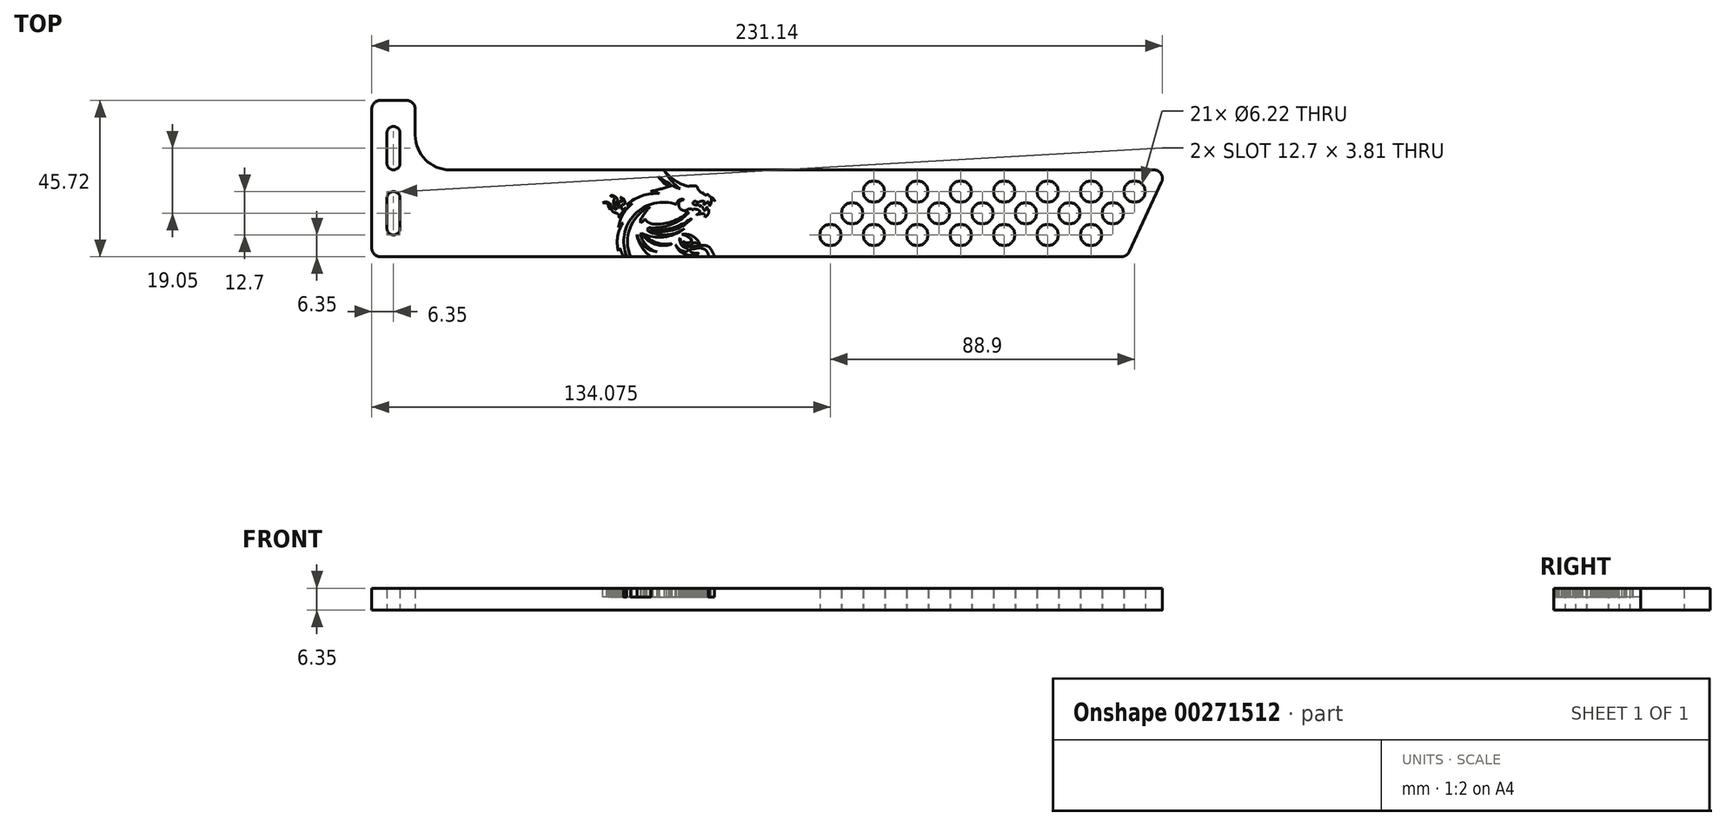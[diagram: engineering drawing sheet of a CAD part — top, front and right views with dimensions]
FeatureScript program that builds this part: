
annotation { "Feature Type Name" : "Feature", "Feature Type Description" : "" }
export const myFeature = defineFeature(function(context is Context, id is Id, definition is map)
    precondition{}
    {
        {
            var Q0;
            Q0=qCreatedBy(makeId("Top.planeOp"),FACE);
            var sketch = newSketch(context, id + "F0", { "sketchPlane" : qUnion([Q0])});
            skLineSegment(sketch, "E0.top", {"start": v(2.54, 45.72) * mm, "end": v(10.16, 45.72) * mm});
            skLineSegment(sketch, "E0.left", {"start": v(0, 2.54) * mm, "end": v(0, 43.18) * mm});
            skLineSegment(sketch, "E0.right", {"start": v(12.7, 35.56) * mm, "end": v(12.7, 43.18) * mm});
            skLineSegment(sketch, "E1.top", {"start": v(22.86, 25.4) * mm, "end": v(228.6, 25.4) * mm});
            skLineSegment(sketch, "E2", {"start": v(2.54, 0) * mm, "end": v(219.12, 0) * mm});
            skArc(sketch, "E3", {"start": v(4.45, 8.25) * mm, "mid": v(6.35, 6.35) * mm, "end": v(8.26, 8.25) * mm});
            skLineSegment(sketch, "E4", {"start": v(4.45, 8.25) * mm, "end": v(4.45, 17.15) * mm});
            skLineSegment(sketch, "E5", {"start": v(8.26, 17.15) * mm, "end": v(8.26, 8.25) * mm});
            skArc(sketch, "E6", {"start": v(8.26, 17.15) * mm, "mid": v(6.35, 19.05) * mm, "end": v(4.45, 17.15) * mm});
            skLineSegment(sketch, "E7.0.1.0", {"start": v(8.26, 36.2) * mm, "end": v(8.26, 27.3) * mm});
            skLineSegment(sketch, "E7.0.1.1", {"start": v(4.45, 27.3) * mm, "end": v(4.45, 36.2) * mm});
            skArc(sketch, "E7.0.1.2", {"start": v(8.26, 36.2) * mm, "mid": v(6.35, 38.1) * mm, "end": v(4.45, 36.2) * mm});
            skArc(sketch, "E7.0.1.3", {"start": v(4.45, 27.3) * mm, "mid": v(6.35, 25.4) * mm, "end": v(8.26, 27.3) * mm});
            skLineSegment(sketch, "E7.direction1", {"start": v(4.45, 8.25) * mm, "end": v(72.67, 8.25) * mm, "construction": true});
            skLineSegment(sketch, "E7.direction2", {"start": v(4.45, 8.25) * mm, "end": v(4.45, 27.3) * mm, "construction": true});
            skPoint(sketch, "E8.visualSharp", {"position": v(0, 45.72) * mm});
            skArc(sketch, "E8.filletArc", {"start": v(2.54, 45.72) * mm, "mid": v(0.74, 44.98) * mm, "end": v(0, 43.18) * mm});
            skPoint(sketch, "E9.visualSharp", {"position": v(12.7, 45.72) * mm});
            skArc(sketch, "E9.filletArc", {"start": v(12.7, 43.18) * mm, "mid": v(11.96, 44.98) * mm, "end": v(10.16, 45.72) * mm});
            skPoint(sketch, "E10.visualSharp", {"position": v(0, 0) * mm});
            skArc(sketch, "E10.filletArc", {"start": v(0, 2.54) * mm, "mid": v(0.74, 0.74) * mm, "end": v(2.54, 0) * mm});
            skPoint(sketch, "E11.visualSharp", {"position": v(12.7, 25.4) * mm});
            skArc(sketch, "E11.filletArc", {"start": v(12.7, 35.56) * mm, "mid": v(15.68, 28.38) * mm, "end": v(22.86, 25.4) * mm});
            skLineSegment(sketch, "E12", {"start": v(221.43, 1.47) * mm, "end": v(230.9, 21.79) * mm});
            skPoint(sketch, "E13.orphan", {"position": v(254, 0) * mm});
            skPoint(sketch, "E14.visualSharp", {"position": v(232.59, 25.4) * mm});
            skArc(sketch, "E14.filletArc", {"start": v(230.9, 21.79) * mm, "mid": v(230.74, 24.22) * mm, "end": v(228.6, 25.4) * mm});
            skPoint(sketch, "E15.visualSharp", {"position": v(220.74, 0) * mm});
            skArc(sketch, "E15.filletArc", {"start": v(219.12, 0) * mm, "mid": v(220.49, 0.4) * mm, "end": v(221.43, 1.47) * mm});
            skCircle(sketch, "E16.1.0.0", {"center": v(210.28, 6.35) * mm, "radius": 3.11 * mm});
            skCircle(sketch, "E16.2.0.0", {"center": v(216.63, 12.7) * mm, "radius": 3.11 * mm});
            skCircle(sketch, "E16.3.0.0", {"center": v(222.98, 19.05) * mm, "radius": 3.11 * mm});
            skLineSegment(sketch, "E17", {"start": v(210.28, 6.35) * mm, "end": v(222.98, 19.05) * mm});
            skCircle(sketch, "E18.1.0.0", {"center": v(203.93, 12.7) * mm, "radius": 3.11 * mm});
            skCircle(sketch, "E18.1.0.1", {"center": v(210.28, 19.05) * mm, "radius": 3.11 * mm});
            skCircle(sketch, "E18.1.0.2", {"center": v(197.58, 6.35) * mm, "radius": 3.11 * mm});
            skCircle(sketch, "E18.2.0.0", {"center": v(191.23, 12.7) * mm, "radius": 3.11 * mm});
            skCircle(sketch, "E18.2.0.1", {"center": v(197.58, 19.05) * mm, "radius": 3.11 * mm});
            skCircle(sketch, "E18.2.0.2", {"center": v(184.88, 6.35) * mm, "radius": 3.11 * mm});
            skLineSegment(sketch, "E18.direction1", {"start": v(216.63, 12.7) * mm, "end": v(203.93, 12.7) * mm, "construction": true});
            skCircle(sketch, "E19.0.3.0", {"center": v(178.53, 12.7) * mm, "radius": 3.11 * mm});
            skCircle(sketch, "E19.2.3.0", {"center": v(184.88, 19.05) * mm, "radius": 3.11 * mm});
            skCircle(sketch, "E19.4.3.0", {"center": v(172.18, 6.35) * mm, "radius": 3.11 * mm});
            skCircle(sketch, "E19.0.4.0", {"center": v(165.83, 12.7) * mm, "radius": 3.11 * mm});
            skCircle(sketch, "E19.2.4.0", {"center": v(172.18, 19.05) * mm, "radius": 3.11 * mm});
            skCircle(sketch, "E19.4.4.0", {"center": v(159.48, 6.35) * mm, "radius": 3.11 * mm});
            skCircle(sketch, "E20.0.5.0", {"center": v(153.13, 12.7) * mm, "radius": 3.11 * mm});
            skCircle(sketch, "E20.2.5.0", {"center": v(159.48, 19.05) * mm, "radius": 3.11 * mm});
            skCircle(sketch, "E20.4.5.0", {"center": v(146.78, 6.35) * mm, "radius": 3.11 * mm});
            skCircle(sketch, "E20.0.6.0", {"center": v(140.43, 12.7) * mm, "radius": 3.11 * mm});
            skCircle(sketch, "E20.2.6.0", {"center": v(146.78, 19.05) * mm, "radius": 3.11 * mm});
            skCircle(sketch, "E20.4.6.0", {"center": v(134.08, 6.35) * mm, "radius": 3.11 * mm});
            skSolve(sketch);
        }
        {
            var Q0;
            Q0=makeQuery(id+"F0.imprint","IMPRINT",FACE,{"disambiguationData":[TD([[makeQuery(id+"F0.imprint","IMPRINT",EDGE,{"derivedFrom":sQuery(id+"F0.wireOp",EDGE,"E0.top")}),-1.0]])]});
            extrude(context, id + "F1", {"entities" : qUnion([Q0]), "depth" : 6.35 * mm});
        }
        {
            var Q0;
            Q0=makeQuery(id+"F1.opExtrude","CAP_FACE",FACE,{"disambiguationData":[OSD([sQuery(id+"F0.wireOp",EDGE,"E0.top"),sQuery(id+"F0.wireOp",EDGE,"E0.left"),sQuery(id+"F0.wireOp",EDGE,"E0.right"),sQuery(id+"F0.wireOp",EDGE,"E1.top"),sQuery(id+"F0.wireOp",EDGE,"E2"),sQuery(id+"F0.wireOp",EDGE,"E3"),sQuery(id+"F0.wireOp",EDGE,"E4"),sQuery(id+"F0.wireOp",EDGE,"E5"),sQuery(id+"F0.wireOp",EDGE,"E6"),sQuery(id+"F0.wireOp",EDGE,"E7.0.1.0"),sQuery(id+"F0.wireOp",EDGE,"E7.0.1.1"),sQuery(id+"F0.wireOp",EDGE,"E7.0.1.2"),sQuery(id+"F0.wireOp",EDGE,"E7.0.1.3"),sQuery(id+"F0.wireOp",EDGE,"E7.0.2.0"),sQuery(id+"F0.wireOp",EDGE,"E7.0.2.1"),sQuery(id+"F0.wireOp",EDGE,"E7.0.2.2"),sQuery(id+"F0.wireOp",EDGE,"E7.0.2.3"),sQuery(id+"F0.wireOp",EDGE,"E8.filletArc"),sQuery(id+"F0.wireOp",EDGE,"E9.filletArc"),sQuery(id+"F0.wireOp",EDGE,"E10.filletArc"),sQuery(id+"F0.wireOp",EDGE,"E11.filletArc"),sQuery(id+"F0.wireOp",EDGE,"XhxQMXou-DX2P-GOic-amz2-HAkX6FaiB0FW"),sQuery(id+"F0.wireOp",EDGE,"E12"),sQuery(id+"F0.wireOp",EDGE,"E14.filletArc"),sQuery(id+"F0.wireOp",EDGE,"E15.filletArc"),sQuery(id+"F0.wireOp",EDGE,"E16.1.0.0"),sQuery(id+"F0.wireOp",EDGE,"E16.2.0.0"),sQuery(id+"F0.wireOp",EDGE,"E16.3.0.0"),sQuery(id+"F0.wireOp",EDGE,"7b475b23-b044-4741-b834-0fa792fca9ea.1.0.0"),sQuery(id+"F0.wireOp",EDGE,"7b475b23-b044-4741-b834-0fa792fca9ea.1.0.1"),sQuery(id+"F0.wireOp",EDGE,"7b475b23-b044-4741-b834-0fa792fca9ea.1.0.2"),sQuery(id+"F0.wireOp",EDGE,"7b475b23-b044-4741-b834-0fa792fca9ea.1.0.3"),sQuery(id+"F0.wireOp",EDGE,"7b475b23-b044-4741-b834-0fa792fca9ea.2.0.0"),sQuery(id+"F0.wireOp",EDGE,"7b475b23-b044-4741-b834-0fa792fca9ea.2.0.1"),sQuery(id+"F0.wireOp",EDGE,"7b475b23-b044-4741-b834-0fa792fca9ea.2.0.2"),sQuery(id+"F0.wireOp",EDGE,"7b475b23-b044-4741-b834-0fa792fca9ea.2.0.3"),sQuery(id+"F0.wireOp",EDGE,"7b475b23-b044-4741-b834-0fa792fca9ea.3.0.0"),sQuery(id+"F0.wireOp",EDGE,"7b475b23-b044-4741-b834-0fa792fca9ea.3.0.1"),sQuery(id+"F0.wireOp",EDGE,"7b475b23-b044-4741-b834-0fa792fca9ea.3.0.2"),sQuery(id+"F0.wireOp",EDGE,"7b475b23-b044-4741-b834-0fa792fca9ea.3.0.3"),sQuery(id+"F0.wireOp",EDGE,"7b475b23-b044-4741-b834-0fa792fca9ea.4.0.0"),sQuery(id+"F0.wireOp",EDGE,"7b475b23-b044-4741-b834-0fa792fca9ea.4.0.1"),sQuery(id+"F0.wireOp",EDGE,"7b475b23-b044-4741-b834-0fa792fca9ea.4.0.2"),sQuery(id+"F0.wireOp",EDGE,"7b475b23-b044-4741-b834-0fa792fca9ea.4.0.3"),sQuery(id+"F0.wireOp",EDGE,"7b475b23-b044-4741-b834-0fa792fca9ea.5.0.0"),sQuery(id+"F0.wireOp",EDGE,"7b475b23-b044-4741-b834-0fa792fca9ea.5.0.1"),sQuery(id+"F0.wireOp",EDGE,"7b475b23-b044-4741-b834-0fa792fca9ea.5.0.2"),sQuery(id+"F0.wireOp",EDGE,"7b475b23-b044-4741-b834-0fa792fca9ea.5.0.3"),sQuery(id+"F0.wireOp",EDGE,"7b475b23-b044-4741-b834-0fa792fca9ea.6.0.0"),sQuery(id+"F0.wireOp",EDGE,"7b475b23-b044-4741-b834-0fa792fca9ea.6.0.1"),sQuery(id+"F0.wireOp",EDGE,"7b475b23-b044-4741-b834-0fa792fca9ea.6.0.2"),sQuery(id+"F0.wireOp",EDGE,"7b475b23-b044-4741-b834-0fa792fca9ea.6.0.3"),sQuery(id+"F0.wireOp",EDGE,"7b475b23-b044-4741-b834-0fa792fca9ea.7.0.0"),sQuery(id+"F0.wireOp",EDGE,"7b475b23-b044-4741-b834-0fa792fca9ea.7.0.1"),sQuery(id+"F0.wireOp",EDGE,"7b475b23-b044-4741-b834-0fa792fca9ea.7.0.2"),sQuery(id+"F0.wireOp",EDGE,"7b475b23-b044-4741-b834-0fa792fca9ea.7.0.3")])],"isStart":false});
            var sketch = newSketch(context, id + "F2", { "sketchPlane" : qUnion([Q0])});
            skLineSegment(sketch, "E21", {"start": v(111.91, 22.02) * mm, "end": v(124.7, 22.02) * mm, "construction": true});
            skLineSegment(sketch, "E22", {"start": v(93.12, 22.02) * mm, "end": v(93.12, 3.84) * mm, "construction": true});
            skEllipticalArc(sketch, "E23", {});
            skEllipticalArc(sketch, "E24", {});
            skEllipticalArc(sketch, "E25", {});
            skEllipticalArc(sketch, "E26", {});
            skEllipticalArc(sketch, "E27", {});
            skLineSegment(sketch, "E28", {"start": v(118.27, 15.08) * mm, "end": v(118.27, 1.13) * mm, "construction": true});
            skLineSegment(sketch, "E29", {"start": v(118.1, 18.88) * mm, "end": v(119.03, 21.76) * mm});
            skLineSegment(sketch, "E30", {"start": v(119.18, 21.85) * mm, "end": v(121.5, 21.29) * mm});
            skLineSegment(sketch, "E31", {"start": v(118.65, 18.87) * mm, "end": v(119.4, 21.28) * mm});
            skLineSegment(sketch, "E32", {"start": v(119.4, 21.28) * mm, "end": v(121.42, 20.8) * mm});
            skArc(sketch, "E33", {"start": v(121.42, 20.8) * mm, "mid": v(123.83, 20.65) * mm, "end": v(121.5, 21.29) * mm});
            skPoint(sketch, "E34.visualSharp", {"position": v(119.07, 21.88) * mm});
            skArc(sketch, "E34.filletArc", {"start": v(119.18, 21.85) * mm, "mid": v(119.1, 21.84) * mm, "end": v(119.03, 21.76) * mm});
            skEllipticalArc(sketch, "E35.MirrorC", {});
            skEllipticalArc(sketch, "E36.MirrorC", {});
            skEllipticalArc(sketch, "E37.MirrorC", {});
            skEllipticalArc(sketch, "E38.trimOffspring", {});
            skEllipticalArc(sketch, "E39.trimOffspring", {});
            skEllipticalArc(sketch, "E40.trimOffspring", {});
            skEllipticalArc(sketch, "E41.trimOffspring", {});
            skLineSegment(sketch, "E42", {"start": v(114.26, 4.24) * mm, "end": v(122.28, 4.24) * mm});
            skEllipticalArc(sketch, "E43.trimOffspring", {});
            skEllipticalArc(sketch, "E44.trimOffspring", {});
            const initialGuessF2  = {"E23": [0.11826750014340877, 0.015082236187587153, 1, 0, 0.005703495972769829, 0.0037955942462822865, 0.8087704461165538, 1.5034823753486115], "E24": [0.11324217923710486, 0.016877323040055132, 0.6434269031423131, 0.7655075573191243, 0.0014490525433377987, 0.001291077385108787, 6.111264569809005, 3.417254100186137], "E25": [0.11827889440944792, 0.009972261073122948, 0, -1, 0.005924312397835806, 0.003007138479654591, 4.399738749622363, 4.432740366885451], "E26": [0.11598712096354366, 0.008977077922474014, -0.9787598014009283, -0.20501036842466144, 0.0019139277871180575, 0.002698036256528401, 4.736724992915178, 1.238121732901221], "E27": [0.11594034994384646, 0.004500067601035371, 0, 1, 0.001621391624212265, 0.0017068755273229488, 6.251739863279235, 1.7313232782154366], "E35.MirrorC": [0.12054787932327389, 0.008977077922474014, 0.9787598014009283, -0.20501036842466142, 0.0019139277871180575, 0.002698036256528401, 5.058073293251867, 1.5337046518671746], "E36.MirrorC": [0.1205946503429711, 0.004500067601035371, 0, 1, 0.001621391624212265, 0.0017068755273229488, 4.551862028964148, 0.017952745052430608], "E37.MirrorC": [0.12329282104971269, 0.016877323040055126, -0.6434269031423131, 0.7655075573191243, 0.0014490525433377987, 0.001291077385108787, 2.865931206993587, 0.1719207373705861], "E38.trimOffspring": [0.11826750014340877, 0.015082236187587153, 1, 0, 0.005703495972769829, 0.0037955942462822865, 3.009051899793022, 4.189151464437954], "E39.trimOffspring": [0.11826750014340878, 0.015082236187587153, 1, 0, 0.005703495972769829, 0.0037955942462822865, 5.239969362590084, 0.13254075379676966], "E40.trimOffspring": [0.11827889440944792, 0.009972261073122948, 0, -1, 0.005924312397835806, 0.003007138479654591, 1.849384891635883, 1.8849135611477357], "E41.trimOffspring": [0.11827889440944792, 0.009972261073122948, 0, -1, 0.005924312397835806, 0.003007138479654591, 5.36960796932527, 5.420151204194051], "E43.trimOffspring": [0.11827889440944721, 0.009972261073122518, 0, -1, 0.005924312397837639, 0.003007138479654591, 0.8631541220241196, 0.9149872669766339], "E44.trimOffspring": [0.11826750014340877, 0.015082236187587153, 1, 0, 0.005703495972769829, 0.0037955942462822865, 1.6014334170188662, 2.332822207473239]};
            skSetInitialGuess(sketch, initialGuessF2);
            skSolve(sketch);
        }
        {
            var Q0;
            Q0=makeQuery(id+"F2.imprint","IMPRINT",FACE,{"disambiguationData":[TD([[makeQuery(id+"F2.imprint","IMPRINT",EDGE,{"derivedFrom":makeQuery(id+"F1.opExtrude","CAP_EDGE",EDGE,{"disambiguationData":[OSD([sQuery(id+"F0.wireOp",EDGE,"E0.top")])],"isStart":false})}),-1.0]])]});
            var sketch = newSketch(context, id + "F3", { "sketchPlane" : qUnion([Q0])});
            skArc(sketch, "E45", {"start": v(72.48, 2.55) * mm, "mid": v(73.02, 1.27) * mm, "end": v(73.6, 0) * mm});
            skArc(sketch, "E46", {"start": v(72.48, 2.55) * mm, "mid": v(72.2, 2.15) * mm, "end": v(72.13, 1.67) * mm});
            skArc(sketch, "E47", {"start": v(73.48, 9.82) * mm, "mid": v(71.88, 5.9) * mm, "end": v(72.13, 1.67) * mm});
            skArc(sketch, "E48", {"start": v(73.48, 9.82) * mm, "mid": v(72.63, 9.33) * mm, "end": v(72.13, 8.48) * mm});
            skArc(sketch, "E49", {"start": v(76.2, 15.57) * mm, "mid": v(73.43, 12.44) * mm, "end": v(72.13, 8.48) * mm});
            skArc(sketch, "E50", {"start": v(74.57, 15.13) * mm, "mid": v(75.39, 15.33) * mm, "end": v(76.2, 15.57) * mm});
            skArc(sketch, "E51", {"start": v(84.06, 18.47) * mm, "mid": v(78.96, 17.82) * mm, "end": v(74.57, 15.13) * mm});
            skArc(sketch, "E52", {"start": v(84.06, 18.47) * mm, "mid": v(82.8, 18.96) * mm, "end": v(81.44, 19.07) * mm});
            skArc(sketch, "E53", {"start": v(81.44, 19.07) * mm, "mid": v(84.66, 19.87) * mm, "end": v(87.8, 20.9) * mm});
            skArc(sketch, "E54", {"start": v(87.8, 20.9) * mm, "mid": v(88.9, 20.26) * mm, "end": v(90.15, 19.94) * mm});
            skArc(sketch, "E55", {"start": v(95.08, 20.56) * mm, "mid": v(93.83, 20.76) * mm, "end": v(92.58, 20.56) * mm});
            skArc(sketch, "E56", {"start": v(95.08, 20.56) * mm, "mid": v(95.57, 19.48) * mm, "end": v(96.43, 18.66) * mm});
            skArc(sketch, "E57", {"start": v(96.43, 18.66) * mm, "mid": v(96.74, 18.59) * mm, "end": v(97.05, 18.66) * mm});
            skArc(sketch, "E58", {"start": v(97.05, 18.66) * mm, "mid": v(97.3, 18.12) * mm, "end": v(97.9, 18.09) * mm});
            skArc(sketch, "E59", {"start": v(98.6, 17.93) * mm, "mid": v(98.29, 18.15) * mm, "end": v(97.9, 18.09) * mm});
            skArc(sketch, "E60", {"start": v(98.6, 17.93) * mm, "mid": v(98.87, 17.55) * mm, "end": v(99.31, 17.38) * mm});
            skArc(sketch, "E61", {"start": v(100.3, 16.31) * mm, "mid": v(99.87, 16.9) * mm, "end": v(99.31, 17.38) * mm});
            skArc(sketch, "E62", {"start": v(100.3, 16.31) * mm, "mid": v(99.8, 16.7) * mm, "end": v(99.25, 17.03) * mm});
            skArc(sketch, "E63", {"start": v(98.72, 14.77) * mm, "mid": v(99.23, 15.84) * mm, "end": v(99.25, 17.03) * mm});
            skArc(sketch, "E64", {"start": v(98.72, 14.77) * mm, "mid": v(98.63, 15.5) * mm, "end": v(98.33, 16.16) * mm});
            skArc(sketch, "E65", {"start": v(96.94, 15.24) * mm, "mid": v(97.72, 15.58) * mm, "end": v(98.33, 16.16) * mm});
            skArc(sketch, "E66", {"start": v(96.94, 15.24) * mm, "mid": v(97.2, 15.67) * mm, "end": v(97.25, 16.16) * mm});
            skArc(sketch, "E67", {"start": v(97.25, 16.16) * mm, "mid": v(96.15, 16.17) * mm, "end": v(95.2, 15.6) * mm});
            skArc(sketch, "E68", {"start": v(94.86, 16.31) * mm, "mid": v(95, 15.94) * mm, "end": v(95.2, 15.6) * mm});
            skArc(sketch, "E69", {"start": v(94.86, 16.31) * mm, "mid": v(94.21, 16.16) * mm, "end": v(93.85, 15.6) * mm});
            skArc(sketch, "E70", {"start": v(93.85, 15.6) * mm, "mid": v(94.6, 15.13) * mm, "end": v(95.47, 15.24) * mm});
            skArc(sketch, "E71", {"start": v(95.47, 15.24) * mm, "mid": v(95.71, 14.96) * mm, "end": v(95.96, 14.69) * mm});
            skArc(sketch, "E72", {"start": v(95.96, 14.69) * mm, "mid": v(96.01, 14.89) * mm, "end": v(96.06, 15.1) * mm});
            skArc(sketch, "E73", {"start": v(97.2, 13.47) * mm, "mid": v(96.74, 14.35) * mm, "end": v(96.06, 15.1) * mm});
            skArc(sketch, "E74", {"start": v(97.2, 13.47) * mm, "mid": v(97.76, 13.88) * mm, "end": v(97.86, 14.56) * mm});
            skArc(sketch, "E75", {"start": v(98.12, 13.58) * mm, "mid": v(98.12, 14.1) * mm, "end": v(97.86, 14.56) * mm});
            skArc(sketch, "E76", {"start": v(98.5, 13.9) * mm, "mid": v(98.3, 13.75) * mm, "end": v(98.12, 13.58) * mm});
            skArc(sketch, "E77", {"start": v(97.3, 11.58) * mm, "mid": v(98.36, 12.5) * mm, "end": v(98.5, 13.9) * mm});
            skArc(sketch, "E78", {"start": v(97.3, 11.58) * mm, "mid": v(97.44, 12.14) * mm, "end": v(97.05, 12.55) * mm});
            skArc(sketch, "E79", {"start": v(97.05, 12.55) * mm, "mid": v(95.97, 12.5) * mm, "end": v(94.93, 12.24) * mm});
            skArc(sketch, "E80", {"start": v(94.93, 12.24) * mm, "mid": v(95.54, 12.7) * mm, "end": v(95.96, 13.33) * mm});
            skArc(sketch, "E81", {"start": v(95.96, 13.33) * mm, "mid": v(95.11, 13.82) * mm, "end": v(94.13, 13.9) * mm});
            skArc(sketch, "E82", {"start": v(93.51, 13.9) * mm, "mid": v(93.82, 13.75) * mm, "end": v(94.13, 13.9) * mm});
            skArc(sketch, "E83", {"start": v(93.51, 13.9) * mm, "mid": v(92.78, 13.98) * mm, "end": v(92.12, 13.66) * mm});
            skArc(sketch, "E84", {"start": v(89.89, 15.95) * mm, "mid": v(90.18, 14) * mm, "end": v(92.12, 13.66) * mm});
            skArc(sketch, "E85", {"start": v(91.29, 16.73) * mm, "mid": v(90.53, 16.45) * mm, "end": v(89.89, 15.95) * mm});
            skArc(sketch, "E86", {"start": v(91.29, 16.73) * mm, "mid": v(89.81, 16.56) * mm, "end": v(89.12, 15.24) * mm});
            skArc(sketch, "E87", {"start": v(89.12, 15.24) * mm, "mid": v(76.85, 12.38) * mm, "end": v(74.54, 0) * mm});
            skArc(sketch, "E88", {"start": v(81.27, 14.56) * mm, "mid": v(75.52, 8.41) * mm, "end": v(75.62, 0) * mm});
            skArc(sketch, "E89", {"start": v(81.27, 14.56) * mm, "mid": v(79.82, 12.75) * mm, "end": v(78.6, 10.79) * mm});
            skArc(sketch, "E90", {"start": v(78.6, 10.79) * mm, "mid": v(78.6, 10.37) * mm, "end": v(78.6, 9.95) * mm});
            skArc(sketch, "E91", {"start": v(78.6, 9.95) * mm, "mid": v(79.36, 10.39) * mm, "end": v(79.86, 11.1) * mm});
            skArc(sketch, "E92", {"start": v(79.83, 11.04) * mm, "mid": v(80.95, 9.98) * mm, "end": v(82.43, 9.53) * mm});
            skArc(sketch, "E93", {"start": v(82.43, 9.53) * mm, "mid": v(87.75, 10.23) * mm, "end": v(92.36, 13) * mm});
            skArc(sketch, "E94", {"start": v(92.5, 12.72) * mm, "mid": v(92.58, 12.93) * mm, "end": v(92.36, 13) * mm});
            skArc(sketch, "E95", {"start": v(81.5, 8.47) * mm, "mid": v(87.47, 9.38) * mm, "end": v(92.5, 12.72) * mm});
            skArc(sketch, "E96", {"start": v(81.5, 8.47) * mm, "mid": v(80.92, 8.38) * mm, "end": v(80.48, 8) * mm});
            skArc(sketch, "E97", {"start": v(80.48, 8) * mm, "mid": v(81.22, 7.23) * mm, "end": v(82.22, 6.86) * mm});
            skArc(sketch, "E98", {"start": v(82.22, 6.86) * mm, "mid": v(86.99, 6.5) * mm, "end": v(91.44, 8.24) * mm});
            skArc(sketch, "E99", {"start": v(78.89, 6.86) * mm, "mid": v(85.36, 5.76) * mm, "end": v(91.44, 8.24) * mm});
            skArc(sketch, "E100", {"start": v(81.76, 8) * mm, "mid": v(87.85, 8.39) * mm, "end": v(93.3, 11.12) * mm});
            skArc(sketch, "E101", {"start": v(93.41, 10.93) * mm, "mid": v(93.38, 11.04) * mm, "end": v(93.3, 11.12) * mm});
            skArc(sketch, "E102", {"start": v(81.76, 7.58) * mm, "mid": v(88, 7.78) * mm, "end": v(93.41, 10.93) * mm});
            skArc(sketch, "E103", {"start": v(81.76, 8) * mm, "mid": v(81.68, 7.79) * mm, "end": v(81.76, 7.58) * mm});
            skArc(sketch, "E104", {"start": v(79.94, 6.17) * mm, "mid": v(79.57, 6.23) * mm, "end": v(79.57, 5.86) * mm});
            skArc(sketch, "E105", {"start": v(79.94, 6.17) * mm, "mid": v(83.37, 4.05) * mm, "end": v(87.4, 3.77) * mm});
            skArc(sketch, "E106", {"start": v(87.4, 3.59) * mm, "mid": v(87.56, 3.68) * mm, "end": v(87.4, 3.77) * mm});
            skArc(sketch, "E107", {"start": v(79.57, 5.86) * mm, "mid": v(83.15, 3.57) * mm, "end": v(87.4, 3.59) * mm});
            skArc(sketch, "E108", {"start": v(78.89, 6.86) * mm, "mid": v(78.6, 6.58) * mm, "end": v(78.62, 6.17) * mm});
            skArc(sketch, "E109", {"start": v(78.62, 6.17) * mm, "mid": v(80.41, 3.18) * mm, "end": v(83.4, 1.4) * mm});
            skArc(sketch, "E110", {"start": v(77.5, 6.46) * mm, "mid": v(79.67, 3.01) * mm, "end": v(83.4, 1.4) * mm});
            skArc(sketch, "E111", {"start": v(77.5, 6.46) * mm, "mid": v(78.93, 2.81) * mm, "end": v(81.64, 0) * mm});
            skArc(sketch, "E112", {"start": v(88.76, 3.62) * mm, "mid": v(89.86, 2.2) * mm, "end": v(91.52, 1.5) * mm});
            skArc(sketch, "E113", {"start": v(91.52, 1.5) * mm, "mid": v(92.3, 1.69) * mm, "end": v(92.08, 2.46) * mm});
            skArc(sketch, "E114", {"start": v(90.1, 5.53) * mm, "mid": v(90.44, 3.57) * mm, "end": v(92.08, 2.46) * mm});
            skArc(sketch, "E115", {"start": v(90.1, 5.53) * mm, "mid": v(91.4, 3.4) * mm, "end": v(93.86, 2.93) * mm});
            skArc(sketch, "E116", {"start": v(96.06, 3.2) * mm, "mid": v(94.95, 3.1) * mm, "end": v(93.86, 2.93) * mm});
            skArc(sketch, "E117", {"start": v(98.65, 2.8) * mm, "mid": v(97.4, 3.3) * mm, "end": v(96.06, 3.2) * mm});
            skArc(sketch, "E118", {"start": v(100.16, 0) * mm, "mid": v(99.57, 1.5) * mm, "end": v(98.65, 2.8) * mm});
            skArc(sketch, "E119", {"start": v(98.4, 0) * mm, "mid": v(97.73, 1.81) * mm, "end": v(95.92, 2.47) * mm});
            skArc(sketch, "E120", {"start": v(95.92, 2.47) * mm, "mid": v(95.1, 2.48) * mm, "end": v(94.3, 2.3) * mm});
            skArc(sketch, "E121", {"start": v(93.11, 2.3) * mm, "mid": v(93.7, 2.28) * mm, "end": v(94.3, 2.3) * mm});
            skArc(sketch, "E122", {"start": v(93.11, 2.3) * mm, "mid": v(93.08, 1.88) * mm, "end": v(93.2, 1.46) * mm});
            skArc(sketch, "E123", {"start": v(93.2, 1.46) * mm, "mid": v(94.28, 1.05) * mm, "end": v(95.45, 1.07) * mm});
            skArc(sketch, "E124", {"start": v(95.45, 0.88) * mm, "mid": v(95.5, 0.98) * mm, "end": v(95.45, 1.07) * mm});
            skArc(sketch, "E125", {"start": v(88.76, 3.62) * mm, "mid": v(91.49, 0.73) * mm, "end": v(95.45, 0.88) * mm});
            skArc(sketch, "E126", {"start": v(95.92, 3.62) * mm, "mid": v(93.77, 6) * mm, "end": v(90.6, 6.54) * mm});
            skArc(sketch, "E127", {"start": v(93.57, 4.95) * mm, "mid": v(92.22, 5.98) * mm, "end": v(90.6, 6.54) * mm});
            skArc(sketch, "E128", {"start": v(91.26, 4.41) * mm, "mid": v(92.56, 4.05) * mm, "end": v(93.57, 4.95) * mm});
            skArc(sketch, "E129", {"start": v(91.26, 4.41) * mm, "mid": v(91.11, 4.41) * mm, "end": v(91.12, 4.27) * mm});
            skArc(sketch, "E130", {"start": v(91.12, 4.27) * mm, "mid": v(92.32, 3.44) * mm, "end": v(93.78, 3.34) * mm});
            skArc(sketch, "E131", {"start": v(93.78, 4.06) * mm, "mid": v(93.56, 3.7) * mm, "end": v(93.78, 3.34) * mm});
            skArc(sketch, "E132", {"start": v(95.92, 3.62) * mm, "mid": v(94.88, 4) * mm, "end": v(93.78, 4.06) * mm});
            skArc(sketch, "E133", {"start": v(84.21, 23.14) * mm, "mid": v(83.97, 23.23) * mm, "end": v(84.05, 22.99) * mm});
            skArc(sketch, "E134", {"start": v(84.21, 23.14) * mm, "mid": v(85.74, 22.13) * mm, "end": v(87.38, 21.29) * mm});
            skArc(sketch, "E135", {"start": v(86.8, 20.74) * mm, "mid": v(87.15, 20.95) * mm, "end": v(87.38, 21.29) * mm});
            skArc(sketch, "E136", {"start": v(86.16, 20.9) * mm, "mid": v(86.46, 20.76) * mm, "end": v(86.8, 20.74) * mm});
            skArc(sketch, "E137", {"start": v(84.05, 22.99) * mm, "mid": v(85.07, 21.9) * mm, "end": v(86.16, 20.9) * mm});
            skLineSegment(sketch, "E138", {"start": v(98.4, 0) * mm, "end": v(100.16, 0) * mm});
            skArc(sketch, "E139", {"start": v(69.99, 17.9) * mm, "mid": v(69.85, 17.8) * mm, "end": v(69.97, 17.67) * mm});
            skArc(sketch, "E140", {"start": v(71.91, 16.42) * mm, "mid": v(71.24, 17.54) * mm, "end": v(69.99, 17.9) * mm});
            skArc(sketch, "E141", {"start": v(71.91, 16.42) * mm, "mid": v(71.73, 16.38) * mm, "end": v(71.62, 16.24) * mm});
            skArc(sketch, "E142", {"start": v(71.62, 16.24) * mm, "mid": v(71.71, 15.22) * mm, "end": v(72.16, 14.3) * mm});
            skArc(sketch, "E143", {"start": v(72.16, 14.3) * mm, "mid": v(72.31, 14.33) * mm, "end": v(72.34, 14.48) * mm});
            skArc(sketch, "E144", {"start": v(72.34, 15.91) * mm, "mid": v(72.26, 15.2) * mm, "end": v(72.34, 14.48) * mm});
            skArc(sketch, "E145", {"start": v(72.54, 16.28) * mm, "mid": v(72.42, 16.1) * mm, "end": v(72.34, 15.91) * mm});
            skArc(sketch, "E146", {"start": v(73.2, 16.04) * mm, "mid": v(72.9, 16.23) * mm, "end": v(72.54, 16.28) * mm});
            skArc(sketch, "E147", {"start": v(73.2, 16.04) * mm, "mid": v(73.32, 16.3) * mm, "end": v(73.28, 16.58) * mm});
            skArc(sketch, "E148", {"start": v(73.28, 16.58) * mm, "mid": v(72.99, 17.02) * mm, "end": v(72.6, 17.38) * mm});
            skArc(sketch, "E149", {"start": v(74.03, 15.76) * mm, "mid": v(73.63, 16.85) * mm, "end": v(72.6, 17.38) * mm});
            skArc(sketch, "E150", {"start": v(73.4, 15.24) * mm, "mid": v(73.83, 15.36) * mm, "end": v(74.03, 15.76) * mm});
            skArc(sketch, "E151", {"start": v(73.4, 15.24) * mm, "mid": v(73.16, 15.18) * mm, "end": v(73.1, 14.94) * mm});
            skArc(sketch, "E152", {"start": v(73.1, 14.94) * mm, "mid": v(72.96, 14.3) * mm, "end": v(73.28, 13.72) * mm});
            skArc(sketch, "E153", {"start": v(73.28, 13.72) * mm, "mid": v(73.64, 13.85) * mm, "end": v(73.92, 14.11) * mm});
            skArc(sketch, "E154", {"start": v(74.2, 14.18) * mm, "mid": v(74.05, 14.18) * mm, "end": v(73.92, 14.11) * mm});
            skArc(sketch, "E155", {"start": v(74.2, 14.01) * mm, "mid": v(74.24, 14.1) * mm, "end": v(74.2, 14.18) * mm});
            skArc(sketch, "E156", {"start": v(74.2, 14.01) * mm, "mid": v(73.12, 12.88) * mm, "end": v(72.39, 11.5) * mm});
            skArc(sketch, "E157", {"start": v(72.22, 11.66) * mm, "mid": v(72.27, 11.55) * mm, "end": v(72.39, 11.5) * mm});
            skArc(sketch, "E158", {"start": v(72.22, 11.66) * mm, "mid": v(72.3, 12.08) * mm, "end": v(72.1, 12.45) * mm});
            skArc(sketch, "E159", {"start": v(72.1, 12.45) * mm, "mid": v(71.4, 12.78) * mm, "end": v(70.67, 13) * mm});
            skArc(sketch, "E160", {"start": v(70.01, 13.82) * mm, "mid": v(70.3, 13.38) * mm, "end": v(70.67, 13) * mm});
            skArc(sketch, "E161", {"start": v(70.01, 13.82) * mm, "mid": v(69.65, 14.05) * mm, "end": v(69.23, 14.14) * mm});
            skArc(sketch, "E162", {"start": v(69.23, 14.14) * mm, "mid": v(69.17, 14.95) * mm, "end": v(68.71, 15.62) * mm});
            skArc(sketch, "E163", {"start": v(68.71, 15.62) * mm, "mid": v(68.1, 15.78) * mm, "end": v(67.48, 15.71) * mm});
            skArc(sketch, "E164", {"start": v(69.23, 15.78) * mm, "mid": v(68.34, 16.02) * mm, "end": v(67.48, 15.71) * mm});
            skPoint(sketch, "E164.startSnap0", {"position": v(68.1, 15.78) * mm});
            skArc(sketch, "E165", {"start": v(70.01, 14.73) * mm, "mid": v(69.8, 15.39) * mm, "end": v(69.23, 15.78) * mm});
            skArc(sketch, "E166", {"start": v(70.01, 14.73) * mm, "mid": v(70.18, 14.45) * mm, "end": v(70.45, 14.27) * mm});
            skArc(sketch, "E167", {"start": v(71.26, 13.82) * mm, "mid": v(70.87, 14.06) * mm, "end": v(70.45, 14.27) * mm});
            skArc(sketch, "E168", {"start": v(71.26, 13.82) * mm, "mid": v(71.49, 13.9) * mm, "end": v(71.45, 14.14) * mm});
            skArc(sketch, "E169", {"start": v(70.9, 17.01) * mm, "mid": v(70.73, 15.5) * mm, "end": v(71.45, 14.14) * mm});
            skArc(sketch, "E170", {"start": v(70.9, 17.01) * mm, "mid": v(71.01, 17.23) * mm, "end": v(70.9, 17.44) * mm});
            skArc(sketch, "E171", {"start": v(70.9, 17.44) * mm, "mid": v(70.46, 17.64) * mm, "end": v(69.97, 17.67) * mm});
            skLineSegment(sketch, "E172", {"start": v(73.6, 0) * mm, "end": v(74.54, 0) * mm});
            skArc(sketch, "E173", {"start": v(85.51, 25.27) * mm, "mid": v(87.5, 22.31) * mm, "end": v(90.15, 19.94) * mm});
            skArc(sketch, "E174", {"start": v(85.51, 25.27) * mm, "mid": v(88.64, 22.3) * mm, "end": v(92.58, 20.56) * mm});
            skLineSegment(sketch, "E175", {"start": v(104.02, 25.4) * mm, "end": v(104.02, 0) * mm});
            skSolve(sketch);
        }
        {
            var Q0;
            Q0=qSketchRegion(id+"F3",true);
            var Q1;
            {var subQ2=sQuery(id+"F3.wireOp",EDGE,"E88");Q1=makeQuery(id+"F3.imprint","IMPRINT",FACE,{"disambiguationData":[TD([[makeQuery(id+"F3.imprint","IMPRINT",EDGE,{"derivedFrom":subQ2}),1.0]])]});}
            extrude(context, id + "F4", {"entities" : qUnion([Q0, Q1]), "operationType" : NewBodyOperationType.REMOVE, "oppositeDirection" : true, "depth" : 2.54 * mm});
        }
    });
